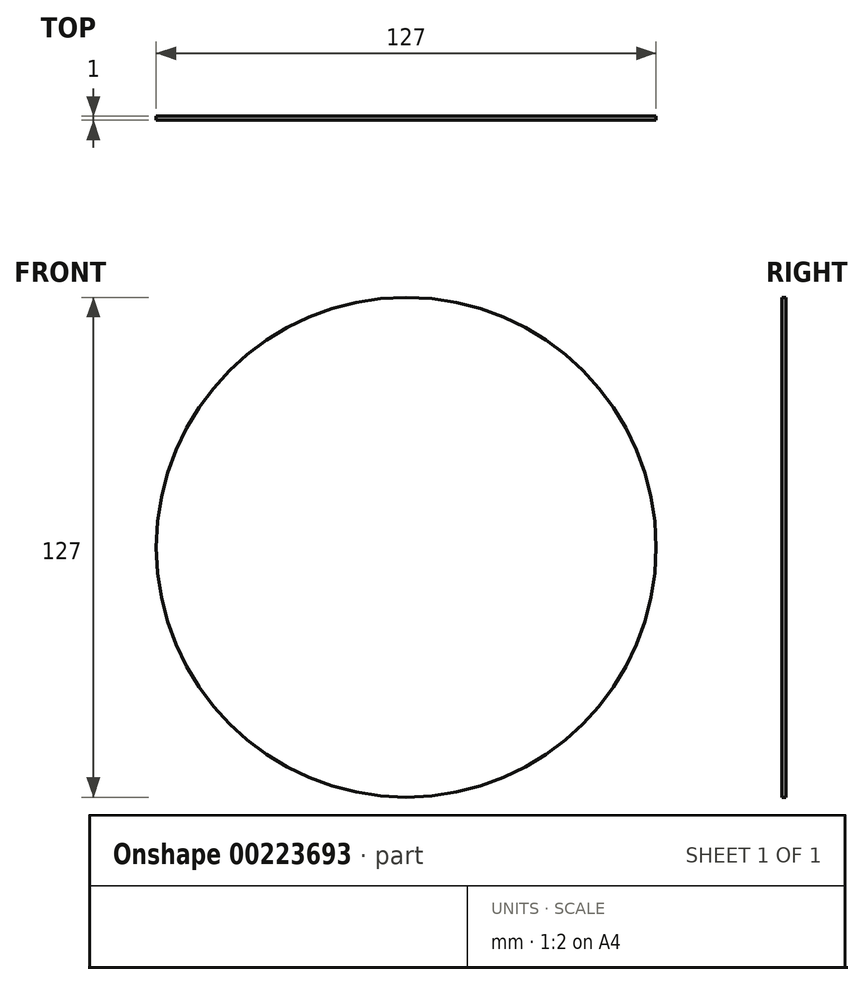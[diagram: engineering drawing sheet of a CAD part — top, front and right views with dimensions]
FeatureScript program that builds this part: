
annotation { "Feature Type Name" : "Feature", "Feature Type Description" : "" }
export const myFeature = defineFeature(function(context is Context, id is Id, definition is map)
    precondition{}
    {
        {
            var Q0;
            Q0=qCreatedBy(makeId("Front.planeOp"),FACE);
            var sketch = newSketch(context, id + "F0", { "sketchPlane" : qUnion([Q0])});
            skCircle(sketch, "E0", {"center": v(1.38, 0) * mm, "radius": 63.5 * mm});
            skSolve(sketch);
        }
        {
            var Q0;
            Q0=qSketchRegion(id+"F0",true);
            extrude(context, id + "F1", {"entities" : qUnion([Q0]), "depth" : 1 * mm});
        }
    });
